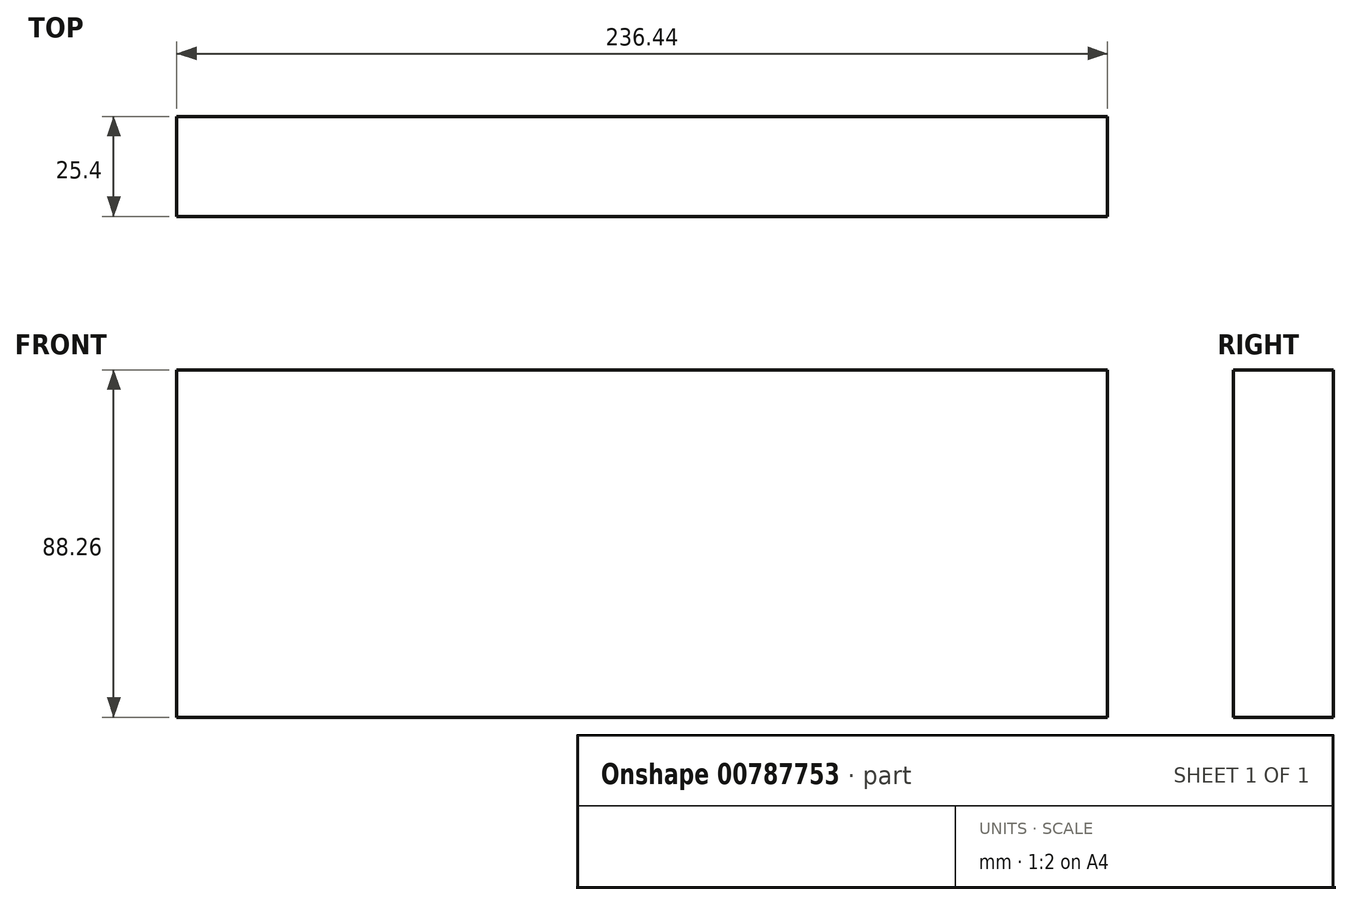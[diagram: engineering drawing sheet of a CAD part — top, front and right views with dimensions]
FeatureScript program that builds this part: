
annotation { "Feature Type Name" : "Feature", "Feature Type Description" : "" }
export const myFeature = defineFeature(function(context is Context, id is Id, definition is map)
    precondition{}
    {
        {
            var Q0;
            Q0=qCreatedBy(makeId("Front.planeOp"),FACE);
            var sketch = newSketch(context, id + "F0", { "sketchPlane" : qUnion([Q0])});
            skLineSegment(sketch, "E0.bottom", {"start": v(-131.48, 47.33) * mm, "end": v(104.96, 47.33) * mm});
            skLineSegment(sketch, "E0.top", {"start": v(-131.48, -40.93) * mm, "end": v(104.96, -40.93) * mm});
            skLineSegment(sketch, "E0.left", {"start": v(-131.48, 47.33) * mm, "end": v(-131.48, -40.93) * mm});
            skLineSegment(sketch, "E0.right", {"start": v(104.96, 47.33) * mm, "end": v(104.96, -40.93) * mm});
            skSolve(sketch);
        }
        {
            var Q0;
            Q0 = qSketchRegion(id + "F0", true);
            extrude(context, id + "F1", {"entities" : qUnion([Q0]), "depth" : 25.4 * mm, "offsetDistance" : 25.4 * mm});
        }
    });
